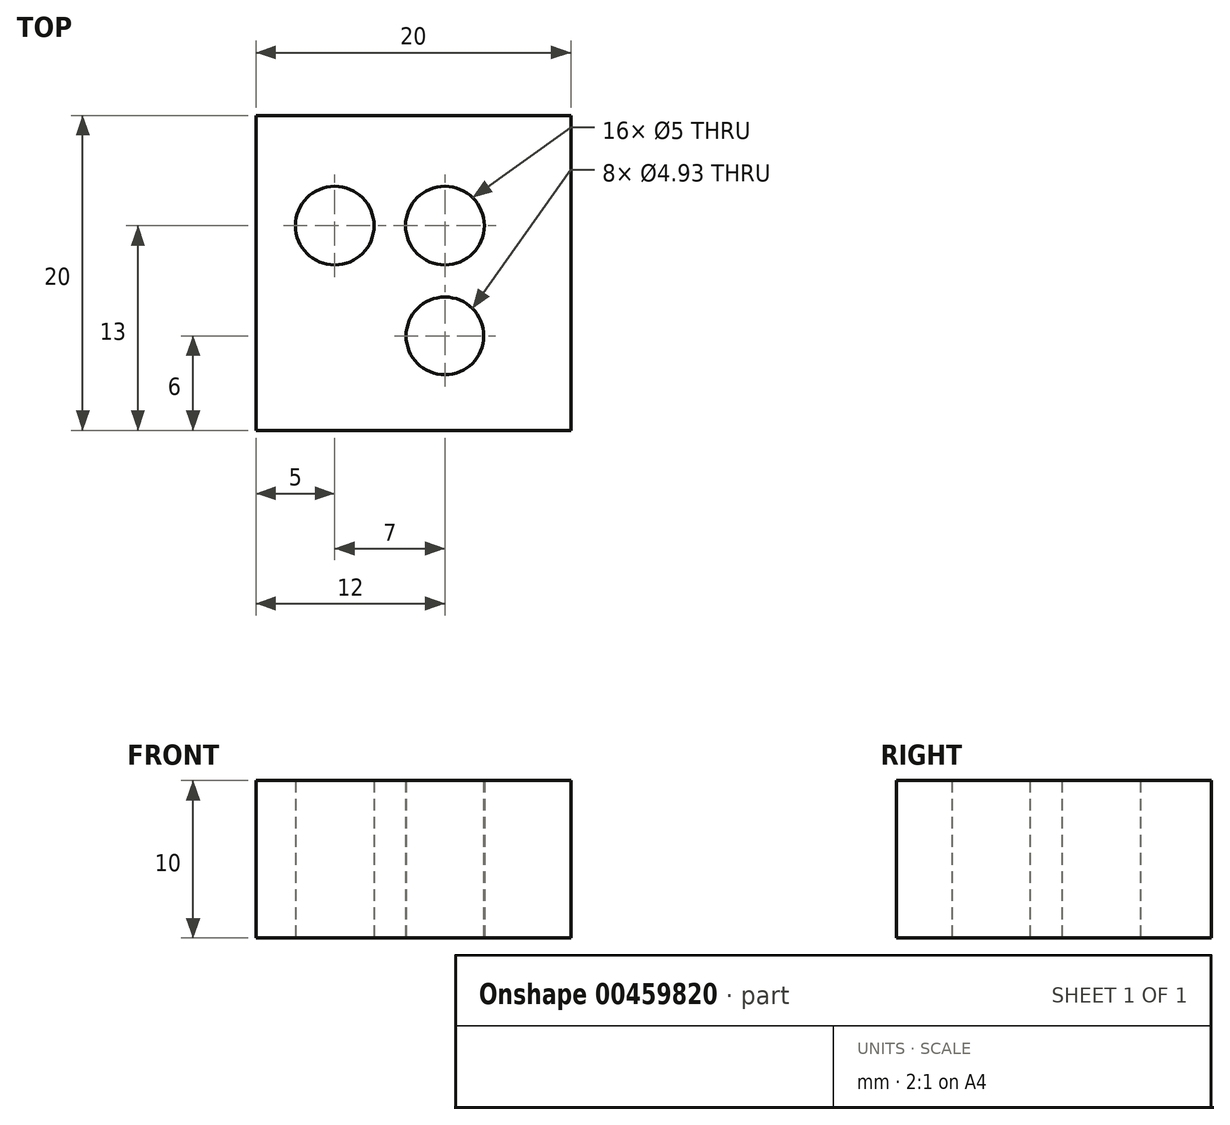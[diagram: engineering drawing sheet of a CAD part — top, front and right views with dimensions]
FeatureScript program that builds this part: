
annotation { "Feature Type Name" : "Feature", "Feature Type Description" : "" }
export const myFeature = defineFeature(function(context is Context, id is Id, definition is map)
    precondition{}
    {
        {
            var Q0;
            Q0=qCreatedBy(makeId("Top.planeOp"),FACE);
            var sketch = newSketch(context, id + "F0", { "sketchPlane" : qUnion([Q0])});
            skLineSegment(sketch, "E0.bottom", {"start": v(0, 0) * mm, "end": v(-20, 0) * mm});
            skLineSegment(sketch, "E0.top", {"start": v(0, 20) * mm, "end": v(-20, 20) * mm});
            skLineSegment(sketch, "E0.left", {"start": v(0, 0) * mm, "end": v(0, 20) * mm});
            skLineSegment(sketch, "E0.right", {"start": v(-20, 0) * mm, "end": v(-20, 20) * mm});
            skCircle(sketch, "E1", {"center": v(-15, 13) * mm, "radius": 2.5 * mm});
            skCircle(sketch, "E2", {"center": v(-8, 13) * mm, "radius": 2.5 * mm});
            skCircle(sketch, "E3", {"center": v(-8, 6) * mm, "radius": 2.47 * mm});
            skSolve(sketch);
        }
        {
            var Q0;
            Q0=makeQuery(id+"F0.imprint","IMPRINT",FACE,{"disambiguationData":[TD([[makeQuery(id+"F0.imprint","IMPRINT",EDGE,{"derivedFrom":sQuery(id+"F0.wireOp",EDGE,"E0.bottom")}),-1.0]])]});
            extrude(context, id + "F1", {"entities" : qUnion([Q0]), "depth" : 10 * mm});
        }
    });
